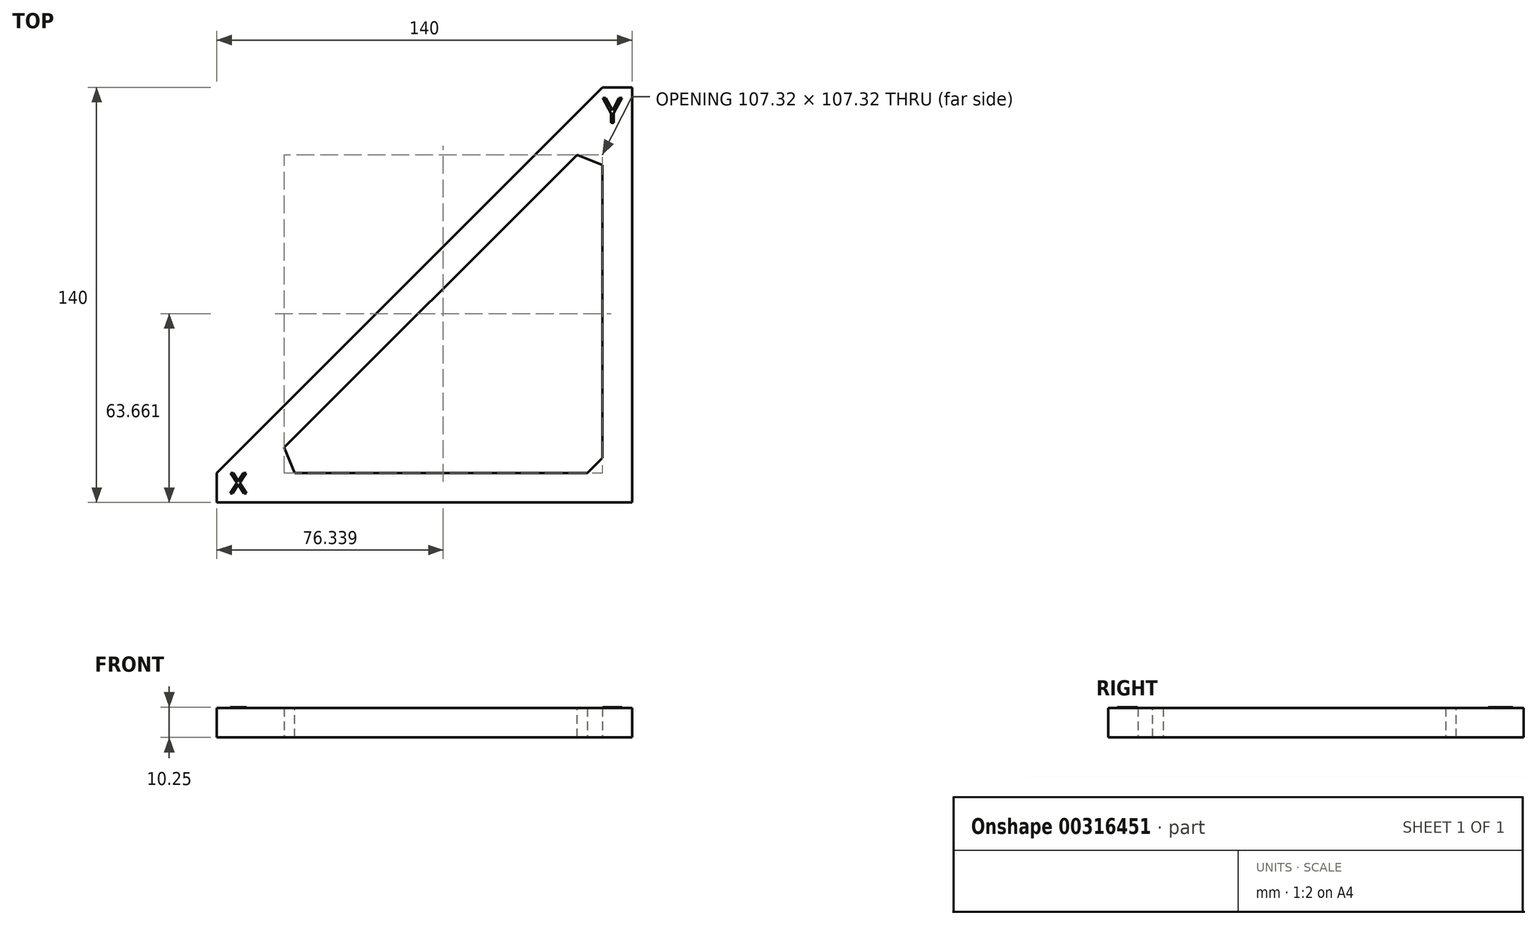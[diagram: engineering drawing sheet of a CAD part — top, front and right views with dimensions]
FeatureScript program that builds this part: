
annotation { "Feature Type Name" : "Feature", "Feature Type Description" : "" }
export const myFeature = defineFeature(function(context is Context, id is Id, definition is map)
    precondition{}
    {
        {
            var Q0;
            Q0=qCreatedBy(makeId("Top.planeOp"),FACE);
            var sketch = newSketch(context, id + "F0", { "sketchPlane" : qUnion([Q0])});
            skLineSegment(sketch, "E0", {"start": v(0, 0) * mm, "end": v(140, 0) * mm});
            skLineSegment(sketch, "E1", {"start": v(140, 0) * mm, "end": v(140, 140) * mm});
            skLineSegment(sketch, "E2", {"start": v(140, 140) * mm, "end": v(130, 140) * mm});
            skLineSegment(sketch, "E3", {"start": v(0, 10) * mm, "end": v(0, 0) * mm});
            skLineSegment(sketch, "E4", {"start": v(130, 140) * mm, "end": v(0, 10) * mm});
            skLineSegment(sketch, "E5.0", {"start": v(130, 10) * mm, "end": v(130, 125.86) * mm});
            skLineSegment(sketch, "E6.0", {"start": v(130, 125.86) * mm, "end": v(14.14, 10) * mm});
            skLineSegment(sketch, "E7.0", {"start": v(14.14, 10) * mm, "end": v(130, 10) * mm});
            skSolve(sketch);
        }
        {
            var Q0;
            Q0 = qSketchRegion(id + "F0", true);
            extrude(context, id + "F1", {"entities" : qUnion([Q0]), "depth" : 10 * mm});
        }
        {
            var Q0;
            Q0=makeQuery(id+"F1.opExtrude","SWEPT_EDGE",EDGE,{"disambiguationData":[OSD([sQuery(id+"F0.wireOp",EDGE,"E5.0"),sQuery(id+"F0.wireOp",EDGE,"E6.0")])]});
            var Q1;
            Q1=makeQuery(id+"F1.opExtrude","SWEPT_EDGE",EDGE,{"disambiguationData":[OSD([sQuery(id+"F0.wireOp",EDGE,"E6.0"),sQuery(id+"F0.wireOp",EDGE,"E7.0")])]});
            var Q2;
            Q2=makeQuery(id+"F1.opExtrude","SWEPT_EDGE",EDGE,{"disambiguationData":[OSD([sQuery(id+"F0.wireOp",EDGE,"E5.0"),sQuery(id+"F0.wireOp",EDGE,"E7.0")])]});
            chamfer(context, id + "F2", {"entities" : qUnion([Q0, Q1, Q2]), "width" : 5 * mm, "tangentPropagation" : true});
        }
        {
            var Q0;
            Q0=makeQuery(id+"F1.opExtrude","CAP_FACE",FACE,{"disambiguationData":[OSD([sQuery(id+"F0.wireOp",EDGE,"E0"),sQuery(id+"F0.wireOp",EDGE,"E1"),sQuery(id+"F0.wireOp",EDGE,"E2"),sQuery(id+"F0.wireOp",EDGE,"E3"),sQuery(id+"F0.wireOp",EDGE,"E4"),sQuery(id+"F0.wireOp",EDGE,"E5.0"),sQuery(id+"F0.wireOp",EDGE,"E6.0"),sQuery(id+"F0.wireOp",EDGE,"E7.0")])],"isStart":false});
            var sketch = newSketch(context, id + "F3", { "sketchPlane" : qUnion([Q0])});
            skText(sketch, "E8", { "text": "X", "fontName": "OpenSans-Regular.ttf"});
            skText(sketch, "E9", { "text": "Y", "fontName": "OpenSans-Regular.ttf"});
            const initialGuessF3  = {"E8": [0.00446, 0.00305, 1, 0, 0.00695], "E9": [0.13013, 0.12811, 1, 0, 0.00838]};
            skSetInitialGuess(sketch, initialGuessF3);
            skSolve(sketch);
        }
        {
            var Q0;
            Q0 = qSketchRegion(id + "F3", true);
            extrude(context, id + "F4", {"entities" : qUnion([Q0]), "operationType" : NewBodyOperationType.ADD, "depth" : 0.25 * mm});
        }
    });
